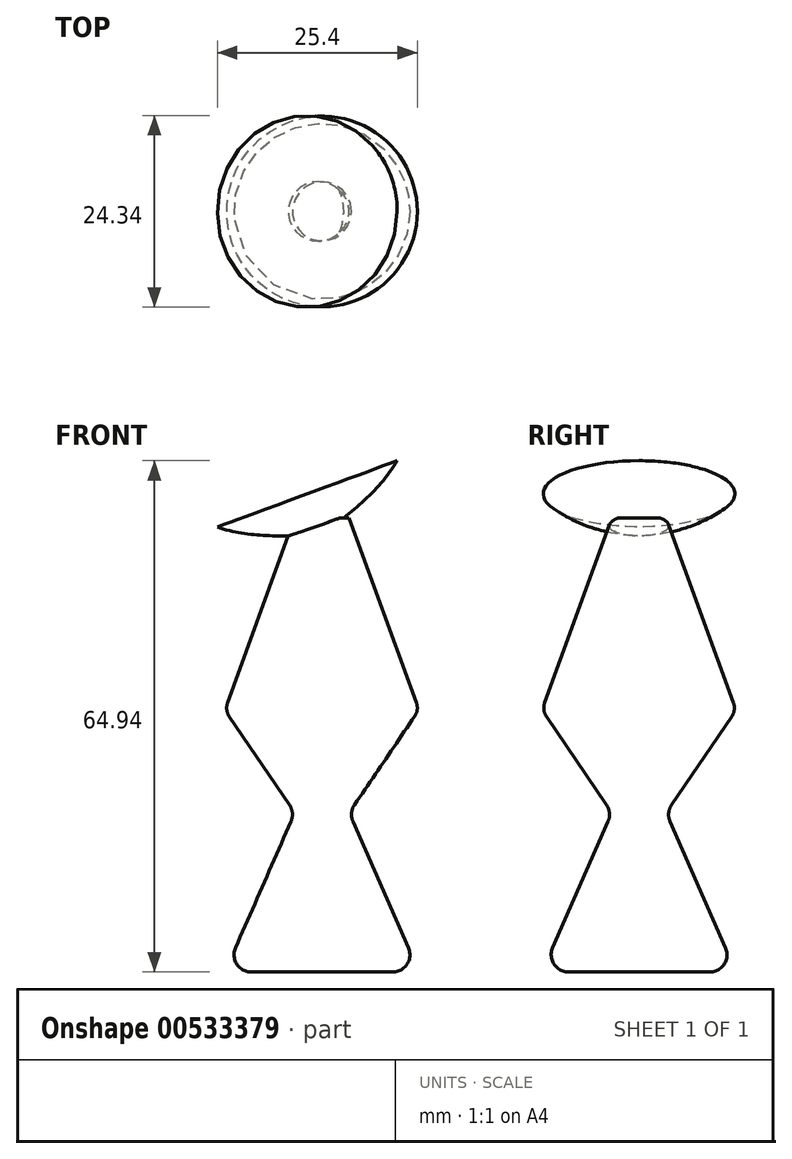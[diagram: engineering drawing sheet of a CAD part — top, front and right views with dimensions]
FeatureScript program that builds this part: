
annotation { "Feature Type Name" : "Feature", "Feature Type Description" : "" }
export const myFeature = defineFeature(function(context is Context, id is Id, definition is map)
    precondition{}
    {
        {
            var Q0;
            Q0=qCreatedBy(makeId("Front.planeOp"),FACE);
            var sketch = newSketch(context, id + "F0", { "sketchPlane" : qUnion([Q0])});
            skLineSegment(sketch, "E0", {"start": v(0, 0) * mm, "end": v(-12.32, 0) * mm});
            skLineSegment(sketch, "E1", {"start": v(-12.32, 0) * mm, "end": v(-3.45, 20.21) * mm});
            skLineSegment(sketch, "E2", {"start": v(-3.45, 20.21) * mm, "end": v(-12.32, 33.27) * mm});
            skLineSegment(sketch, "E3", {"start": v(-12.32, 33.27) * mm, "end": v(-3.45, 57.68) * mm});
            skLineSegment(sketch, "E4", {"start": v(-3.45, 57.68) * mm, "end": v(0, 57.68) * mm});
            skLineSegment(sketch, "E5", {"start": v(0, 57.68) * mm, "end": v(0, 0) * mm});
            skSolve(sketch);
        }
        {
            var Q0;
            Q0 = qSketchRegion(id + "F0", true);
            var Q1;
            Q1=sQuery(id+"F0.wireOp",EDGE,"E5");
            revolve(context, id + "F1", {"surfaceOperationType" : NewSurfaceOperationType.NEW, "entities" : qUnion([Q0]), "axis" : qUnion([Q1]), "revolveType" : RevolveType.FULL});
        }
        {
            var Q0;
            Q0=makeQuery(id+"F1.opRevolve","SWEPT_EDGE",EDGE,{"disambiguationData":[OSD([sQuery(id+"F0.wireOp",EDGE,"E2"),sQuery(id+"F0.wireOp",EDGE,"E3")])]});
            fillet(context, id + "F2", {"entities" : qUnion([Q0]), "radius" : 1.89 * mm, "tangentPropagation" : true, "allowEdgeOverflow" : false});
        }
        {
            var Q0;
            Q0=makeQuery(id+"F1.opRevolve","SWEPT_FACE",FACE,{"disambiguationData":[OSD([sQuery(id+"F0.wireOp",EDGE,"E1")])]});
            fillet(context, id + "F3", {"entities" : qUnion([Q0]), "radius" : 2.17 * mm, "tangentPropagation" : true, "allowEdgeOverflow" : false});
        }
        {
            var Q0;
            Q0=qCreatedBy(makeId("Front.planeOp"),FACE);
            var sketch = newSketch(context, id + "F4", { "sketchPlane" : qUnion([Q0])});
            skFitSpline(sketch, "E6", {"points": [v(0, 55.66) * mm, v(-5.87, 55.4) * mm, v(-13.3, 56.52) * mm], "startDerivative": vector(-12.36, -1.63) * mm, "endDerivative": vector(-14.8, 5.19) * mm});
            skLineSegment(sketch, "E7", {"start": v(-13.3, 56.52) * mm, "end": v(-1.87, 60.73) * mm});
            skLineSegment(sketch, "E8", {"start": v(-1.87, 60.73) * mm, "end": v(0, 55.66) * mm});
            skSolve(sketch);
        }
        {
            var Q0;
            Q0 = qSketchRegion(id + "F4", true);
            var Q1;
            Q1=sQuery(id+"F4.wireOp",EDGE,"E8");
            revolve(context, id + "F5", {"operationType" : NewBodyOperationType.ADD, "surfaceOperationType" : NewSurfaceOperationType.NEW, "entities" : qUnion([Q0]), "axis" : qUnion([Q1]), "revolveType" : RevolveType.FULL});
        }
    });
